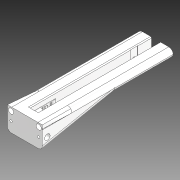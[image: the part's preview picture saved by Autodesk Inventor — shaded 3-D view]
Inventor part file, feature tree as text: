
AUTODESK INVENTOR PART (.ipt)
format: ipt  version: 2020 (Build 240168000, 168)  size: 1,272,320 bytes
history: native  units: in
note: dims shown in document units (in); Inventor stores cm internally (conversion verified against a paired STEP export)
features: other x6, extrude x6, sketch x4, fillet x2, reference x1, imported_body x1
ambient origin geometry x8: Origin, YZ Plane, XZ Plane, XY Plane, X Axis, Y Axis, Z Axis, Center Point
bodies: Solid1 (feature_tree)
feature tree (20):
  other  "Blocks"
  extrude  "Extrusion2"  Depth=0.5625in TaperAngle=0.0deg
  extrude  "Extrusion3"  Depth=0.3543in TaperAngle=0.0deg
  extrude  "Extrusion4"  Depth=0.3937in TaperAngle=0.0deg
  extrude  "Extrusion6"  Depth=0.0787in
  extrude  "Extrusion7"  Depth=0.0787in
  fillet  "Fillet2"  Radius=0.0591in
  extrude  "Extrusion8"  Depth=0.0787in TaperAngle=0.0deg
  fillet  "Fillet3"  Radius=0.0394in
  sketch  "Sketch2"  dims[d3=0.0039in d4=0.5625in d5=0.0in]
  other  "Block1"
  sketch  "Sketch5"  dims[d6=0.185in d7=0.185in d8=0.0984in d9=0.0984in d10=0.1181in d11=0.1181in d17=0.3543in d18=0.0in]
  sketch  "Sketch6"  dims[d19=0.3937in d20=0.0in d27=0.3543in d28=0.0in]
  reference  "Reference1"
  sketch  "Sketch7"  dims[d29=0.1181in d31=0.0394in d32=0.0591in d33=0.0591in d34=0.0787in d35=0.0in d36=0.0394in d37=0.2362in d38=0.575in d39=0.0in d40=0.0787in d0=0.0197in d1=1.9685in d2=0.0197in]
  imported_body  "Base1"
  other  "Block1:1"
  other  "<userpath>\Documents\Drew\Projects\Nerf Aim Assist\ESPER\ETrigger.iam"
  other  "ETrigger.iam"
  other  "MG90servo_body:1"
